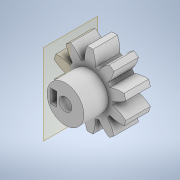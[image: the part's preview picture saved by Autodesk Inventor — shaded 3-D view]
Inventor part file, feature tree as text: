
AUTODESK INVENTOR PART (.ipt)
format: ipt  version: 2020 (Build 240168000, 168)  size: 212,480 bytes
history: native  units: in
note: dims shown in document units (in); Inventor stores cm internally (conversion verified against a paired STEP export)
features: extrude x5, sketch x5, other x2, plane x1
ambient origin geometry x8: Origin, YZ Plane, XZ Plane, XY Plane, X Axis, Y Axis, Z Axis, Center Point
bodies: Solid1 (feature_tree)
feature tree (13):
  extrude  "Extrusion1"  Depth=0.3937in
  other  "Spur Gear Teeth1"
  extrude  "Extrusion2"  Depth=0.3937in TaperAngle=0.0deg
  extrude  "Extrusion3"  Depth=0.3937in TaperAngle=0.0deg
  plane  "Work Plane1"
  extrude  "Extrusion5"  Depth=0.1181in
  extrude  "Extrusion6"  Depth=0.3937in TaperAngle=0.0deg
  sketch  "Sketch1"  dims[d0=0.3937in d1=0.0in d2=1.9685in]
  other  "Spur Gear1"
  sketch  "Sketch2"  dims[d3=0.5906in d4=0.3937in d5=0.0in]
  sketch  "Sketch3"  dims[d6=0.2047in d7=0.3937in d8=0.0in]
  sketch  "Sketch5"  dims[d11=-0.3125in d12=0.1181in]
  sketch  "Sketch6"  dims[d13=0.5906in d14=0.3937in d15=0.0in d17=0.0984in d19=0.1083in d20=0.2165in d21=0.2953in d22=0.0in]
